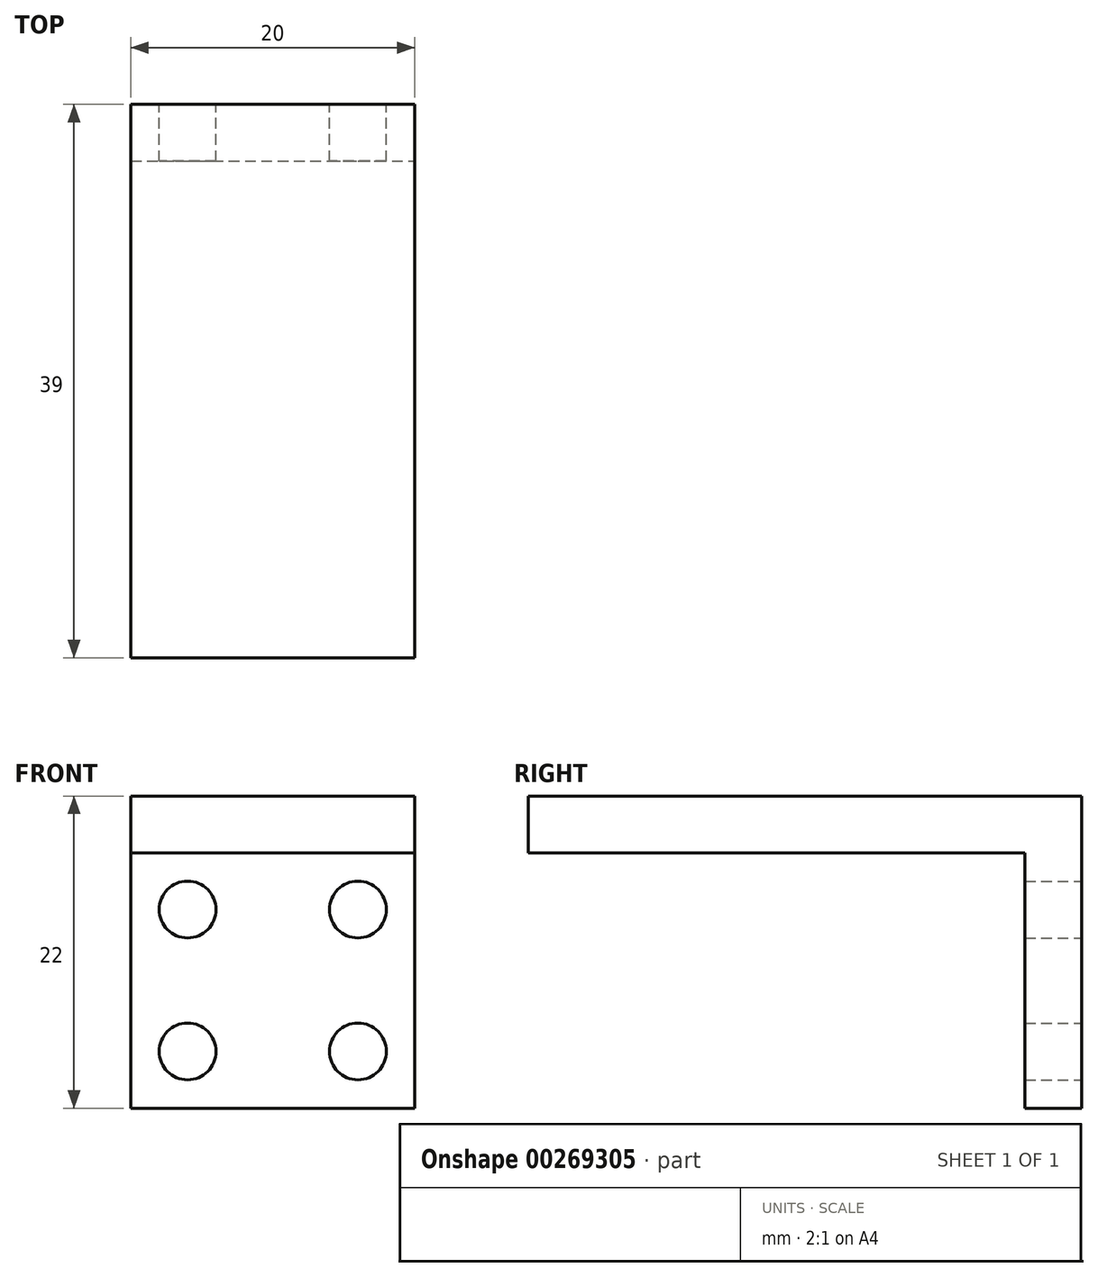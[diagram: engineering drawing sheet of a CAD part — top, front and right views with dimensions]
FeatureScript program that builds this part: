
annotation { "Feature Type Name" : "Feature", "Feature Type Description" : "" }
export const myFeature = defineFeature(function(context is Context, id is Id, definition is map)
    precondition{}
    {
        {
            var Q0;
            Q0=qCreatedBy(makeId("Front.planeOp"),FACE);
            var sketch = newSketch(context, id + "F0", { "sketchPlane" : qUnion([Q0])});
            skCircle(sketch, "E0", {"center": v(6, 5) * mm, "radius": 2 * mm});
            skCircle(sketch, "E1", {"center": v(-6, 5) * mm, "radius": 2 * mm});
            skCircle(sketch, "E2", {"center": v(-6, -5) * mm, "radius": 2 * mm});
            skCircle(sketch, "E3", {"center": v(6, -5) * mm, "radius": 2 * mm});
            skLineSegment(sketch, "E4.bottom", {"start": v(-10, 13) * mm, "end": v(10, 13) * mm});
            skLineSegment(sketch, "E4.top", {"start": v(-10, -9) * mm, "end": v(10, -9) * mm});
            skLineSegment(sketch, "E4.left", {"start": v(-10, 13) * mm, "end": v(-10, -9) * mm});
            skLineSegment(sketch, "E4.right", {"start": v(10, 13) * mm, "end": v(10, -9) * mm});
            skSolve(sketch);
        }
        {
            var Q0;
            Q0=makeQuery(id+"F0.imprint","IMPRINT",FACE,{"disambiguationData":[TD([[makeQuery(id+"F0.imprint","IMPRINT",EDGE,{"derivedFrom":sQuery(id+"F0.wireOp",EDGE,"E0")}),-1.0]])]});
            extrude(context, id + "F1", {"entities" : qUnion([Q0]), "depth" : 4 * mm});
        }
        {
            var Q0;
            Q0=makeQuery(id+"F1.opExtrude","CAP_FACE",FACE,{"disambiguationData":[OSD([sQuery(id+"F0.wireOp",EDGE,"E0"),sQuery(id+"F0.wireOp",EDGE,"E1"),sQuery(id+"F0.wireOp",EDGE,"E2"),sQuery(id+"F0.wireOp",EDGE,"E3"),sQuery(id+"F0.wireOp",EDGE,"E4.bottom"),sQuery(id+"F0.wireOp",EDGE,"E4.top"),sQuery(id+"F0.wireOp",EDGE,"E4.left"),sQuery(id+"F0.wireOp",EDGE,"E4.right")])],"isStart":false});
            var sketch = newSketch(context, id + "F2", { "sketchPlane" : qUnion([Q0])});
            skLineSegment(sketch, "E5.bottom", {"start": v(-10, 13) * mm, "end": v(10, 13) * mm});
            skLineSegment(sketch, "E5.top", {"start": v(-10, 9) * mm, "end": v(10, 9) * mm});
            skLineSegment(sketch, "E5.left", {"start": v(-10, 13) * mm, "end": v(-10, 9) * mm});
            skLineSegment(sketch, "E5.right", {"start": v(10, 13) * mm, "end": v(10, 9) * mm});
            skSolve(sketch);
        }
        {
            var Q0;
            Q0=makeQuery(id+"F2.imprint","IMPRINT",FACE,{"disambiguationData":[TD([[makeQuery(id+"F2.imprint","IMPRINT",EDGE,{"derivedFrom":sQuery(id+"F2.wireOp",EDGE,"E5.bottom")}),-1.0]])]});
            extrude(context, id + "F3", {"entities" : qUnion([Q0]), "operationType" : NewBodyOperationType.ADD, "depth" : 35 * mm});
        }
    });
